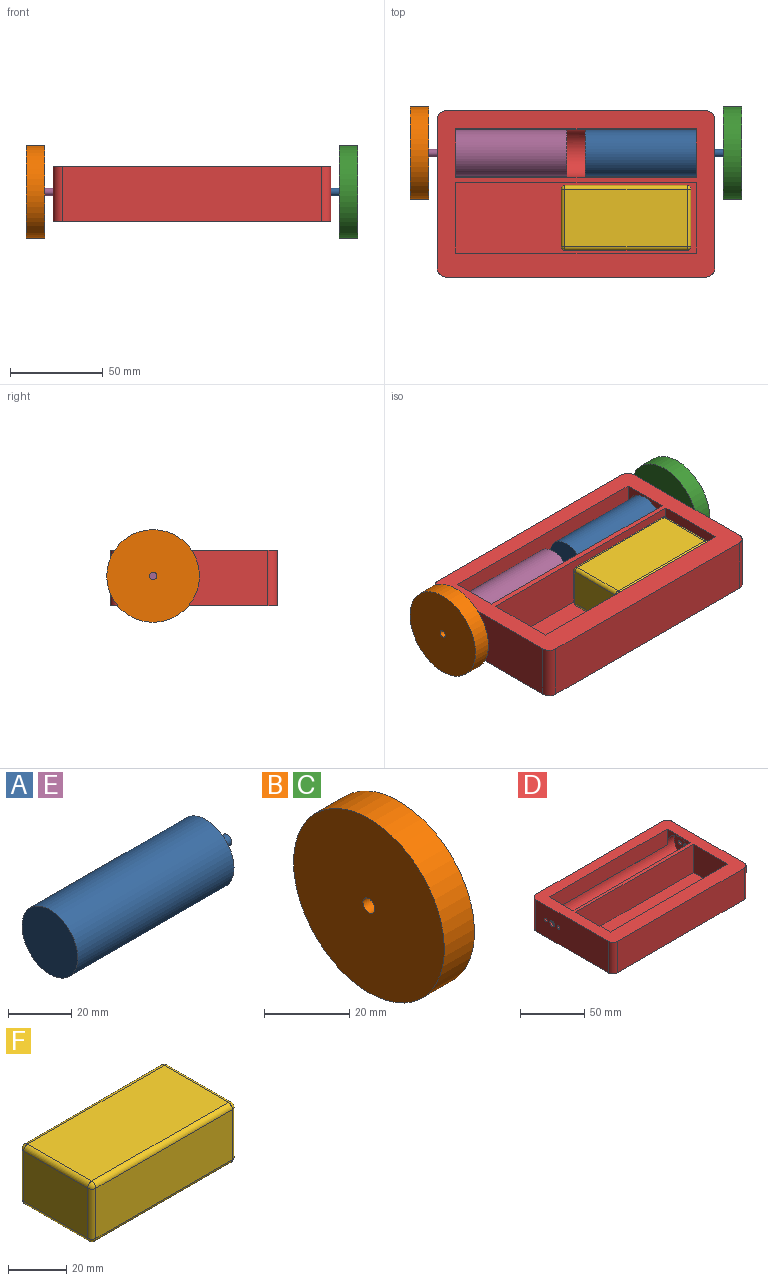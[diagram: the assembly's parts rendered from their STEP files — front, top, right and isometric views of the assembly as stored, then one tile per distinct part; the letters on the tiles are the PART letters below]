
ASSEMBLY  parts=6 mates=5
PART A: 5 faces, bbox 79.5x25x25 mm
  f0: cylinder r=12.5mm len=70mm, axis (-1,0,0), area 5497.8mm2, adj f1,f2
  f1: plane 25x25mm, normal (1,0,0), area 478.3mm2, adj f0,f3
  f2: plane 25x25mm, normal (-1,0,0), area 490.9mm2, adj f0
  f3: cylinder r=2mm len=9.5mm, axis (-1,0,0), area 119.4mm2, adj f1,f4
  f4: plane 4x4mm, normal (1,0,0), area 12.6mm2, adj f3
PART B: 4 faces, bbox 10x50x50 mm
  f0: cylinder r=2mm len=10mm, axis (-1,0,0), area 125.7mm2, adj f2,f3
  f1: cylinder r=25mm len=50mm, axis (-1,0,0), area 1570.8mm2, adj f2,f3
  f2: plane 50x50mm, normal (1,0,0), area 1950.9mm2, adj f0,f1
  f3: plane 50x50mm, normal (-1,0,0), area 1950.9mm2, adj f0,f1
PART C: same geometry as B
PART D: 34 faces, bbox 150x90x30 mm
  f0: plane 150x90mm, normal (0,0,1), area 5158.5mm2, adj f2,f3,f4,f5,f15,f16,f17,f18
  f1: cylinder r=13mm len=146mm, axis (-1,0,0), area 6355.9mm2, adj f10,f14,f19,f20,f22,f23,f24,f26
  f2: plane 140x30mm, normal (0,-1,0), area 4200mm2, adj f0,f6,f15,f18
  f3: plane 80x30mm, normal (1,0,0), area 2366.2mm2, adj f0,f6,f7,f8,f9,f15,f16
  f4: plane 140x30mm, normal (0,1,0), area 4200mm2, adj f0,f6,f16,f17
  f5: plane 80x30mm, normal (-1,0,0), area 2366.2mm2, adj f0,f6,f11,f12,f13,f17,f18
  f6: plane 150x90mm, normal (0,0,-1), area 13478.5mm2, adj f2,f3,f4,f5,f15,f16,f17,f18
  f7: cylinder r=1.5mm len=3mm, axis (1,0,0), area 18.8mm2, adj f3,f10
  f8: cylinder r=1.5mm len=3mm, axis (1,0,0), area 18.8mm2, adj f3,f10
  f9: cylinder r=2.5mm len=5mm, axis (1,0,0), area 31.4mm2, adj f3,f10
  f10: plane 26x26mm, normal (-1,0,0), area 497.2mm2, adj f1,f7,f8,f9
  f11: cylinder r=1.5mm len=3mm, axis (-1,0,0), area 18.8mm2, adj f5,f14
  f12: cylinder r=1.5mm len=3mm, axis (-1,0,0), area 18.8mm2, adj f5,f14
  f13: cylinder r=2.5mm len=5mm, axis (-1,0,0), area 31.4mm2, adj f5,f14
  f14: plane 26x26mm, normal (1,0,0), area 497.2mm2, adj f1,f11,f12,f13
  f15: cylinder r=5mm len=30mm, axis (0,0,1), area 235.6mm2, adj f0,f2,f3,f6
  f16: cylinder r=5mm len=30mm, axis (0,0,-1), area 235.6mm2, adj f0,f3,f4,f6
  f17: cylinder r=5mm len=30mm, axis (0,0,1), area 235.6mm2, adj f0,f4,f5,f6
  f18: cylinder r=5mm len=30mm, axis (0,0,-1), area 235.6mm2, adj f0,f2,f5,f6
  f19: plane 130x0.04mm, normal (0,0,1), area 5mm2, adj f1,f23,f25,f27
  f20: plane 130x0.04mm, normal (0,0,1), area 5mm2, adj f1,f21,f22,f26
  f21: plane 130x15mm, normal (0,1,0), area 1950mm2, adj f0,f20,f22,f24,f26,f28
  f22: plane 1x0.04mm, normal (-1,0,0), area 0mm2, adj f1,f20,f21
  f23: plane 1x0.04mm, normal (-1,0,0), area 0mm2, adj f1,f19,f25
  f24: plane 26x14mm, normal (-1,0,0), area 98.5mm2, adj f0,f1,f21,f25
  f25: plane 130x15mm, normal (0,-1,0), area 1950mm2, adj f0,f19,f23,f24,f27,f28
  f26: plane 1x0.04mm, normal (1,0,0), area 0mm2, adj f1,f20,f21
  f27: plane 1x0.04mm, normal (1,0,0), area 0mm2, adj f1,f19,f25
  f28: plane 26x14mm, normal (1,0,0), area 98.5mm2, adj f0,f1,f21,f25
  f29: plane 38x27mm, normal (1,0,0), area 1026mm2, adj f0,f30,f32,f33
  f30: plane 130x27mm, normal (0,1,0), area 3510mm2, adj f0,f29,f31,f33
  f31: plane 38x27mm, normal (-1,0,0), area 1026mm2, adj f0,f30,f32,f33
  f32: plane 130x27mm, normal (0,-1,0), area 3510mm2, adj f0,f29,f31,f33
  f33: plane 130x38mm, normal (0,0,1), area 4940mm2, adj f29,f30,f31,f32
PART E: same geometry as A
PART F: 26 faces, bbox 70x35x25 mm
  f0: plane 66x21mm, normal (0,-1,0), area 1386mm2, adj f14,f19,f22,f25
  f1: plane 31x21mm, normal (1,0,0), area 651mm2, adj f11,f20,f21,f25
  f2: plane 66x21mm, normal (0,1,0), area 1386mm2, adj f6,f10,f11,f12
  f3: plane 31x21mm, normal (-1,0,0), area 651mm2, adj f6,f9,f13,f14
  f4: plane 66x31mm, normal (0,0,1), area 2046mm2, adj f9,f10,f19,f20
  f5: plane 66x31mm, normal (0,0,-1), area 2046mm2, adj f12,f13,f21,f22
  f6: cylinder r=2mm len=21mm, axis (0,0,1), area 66mm2, adj f2,f3,f7,f8
  f7: sphere r=2mm, area 6.3mm2, adj f6,f9,f10
  f8: sphere r=2mm, area 6.3mm2, adj f6,f12,f13
  f9: cylinder r=2mm len=31mm, axis (0,1,0), area 97.4mm2, adj f3,f4,f7,f15
  f10: cylinder r=2mm len=66mm, axis (1,0,0), area 207.3mm2, adj f2,f4,f7,f16
  f11: cylinder r=2mm len=21mm, axis (0,0,-1), area 66mm2, adj f1,f2,f16,f17
  f12: cylinder r=2mm len=66mm, axis (-1,0,0), area 207.3mm2, adj f2,f5,f8,f17
  f13: cylinder r=2mm len=31mm, axis (0,-1,0), area 97.4mm2, adj f3,f5,f8,f18
  f14: cylinder r=2mm len=21mm, axis (0,0,-1), area 66mm2, adj f0,f3,f15,f18
  f15: sphere r=2mm, area 6.3mm2, adj f9,f14,f19
  f16: sphere r=2mm, area 6.3mm2, adj f10,f11,f20
  f17: sphere r=2mm, area 6.3mm2, adj f11,f12,f21
  f18: sphere r=2mm, area 6.3mm2, adj f13,f14,f22
  f19: cylinder r=2mm len=66mm, axis (-1,0,0), area 207.3mm2, adj f0,f4,f15,f23
  f20: cylinder r=2mm len=31mm, axis (0,-1,0), area 97.4mm2, adj f1,f4,f16,f23
  f21: cylinder r=2mm len=31mm, axis (0,1,0), area 97.4mm2, adj f1,f5,f17,f24
  f22: cylinder r=2mm len=66mm, axis (1,0,0), area 207.3mm2, adj f0,f5,f18,f24
  f23: sphere r=2mm, area 6.3mm2, adj f19,f20,f25
  f24: sphere r=2mm, area 6.3mm2, adj f21,f22,f25
  f25: cylinder r=2mm len=21mm, axis (0,0,1), area 66mm2, adj f0,f1,f23,f24
PLACE A t=(2.43,19.93,4)mm
PLACE B t=(-92.07,19.93,4)mm
PLACE C t=(76.93,19.93,4)mm
PLACE D t=(-2.57,-2.07,-12)mm
PLACE E rot(axis=(0,1,0),180deg) t=(-7.57,19.93,4)mm
PLACE F t=(24.43,-15.07,-9)mm
MATE fastened B.f1 <-> E.f3  axis (-1,0,0) through (-92.07,19.93,4)mm
MATE fastened E.f0 <-> A.f0  axis (1,0,0) through (-7.57,19.93,4)mm
MATE fastened F.f5 <-> D.f33  axis (0,0,-1) through (24.43,-15.07,-9)mm
MATE fastened E.f3 <-> D.f1  axis (1,0,0) through (-77.57,19.93,4)mm
MATE fastened C.f1 <-> A.f3  axis (1,0,0) through (86.93,19.93,4)mm
